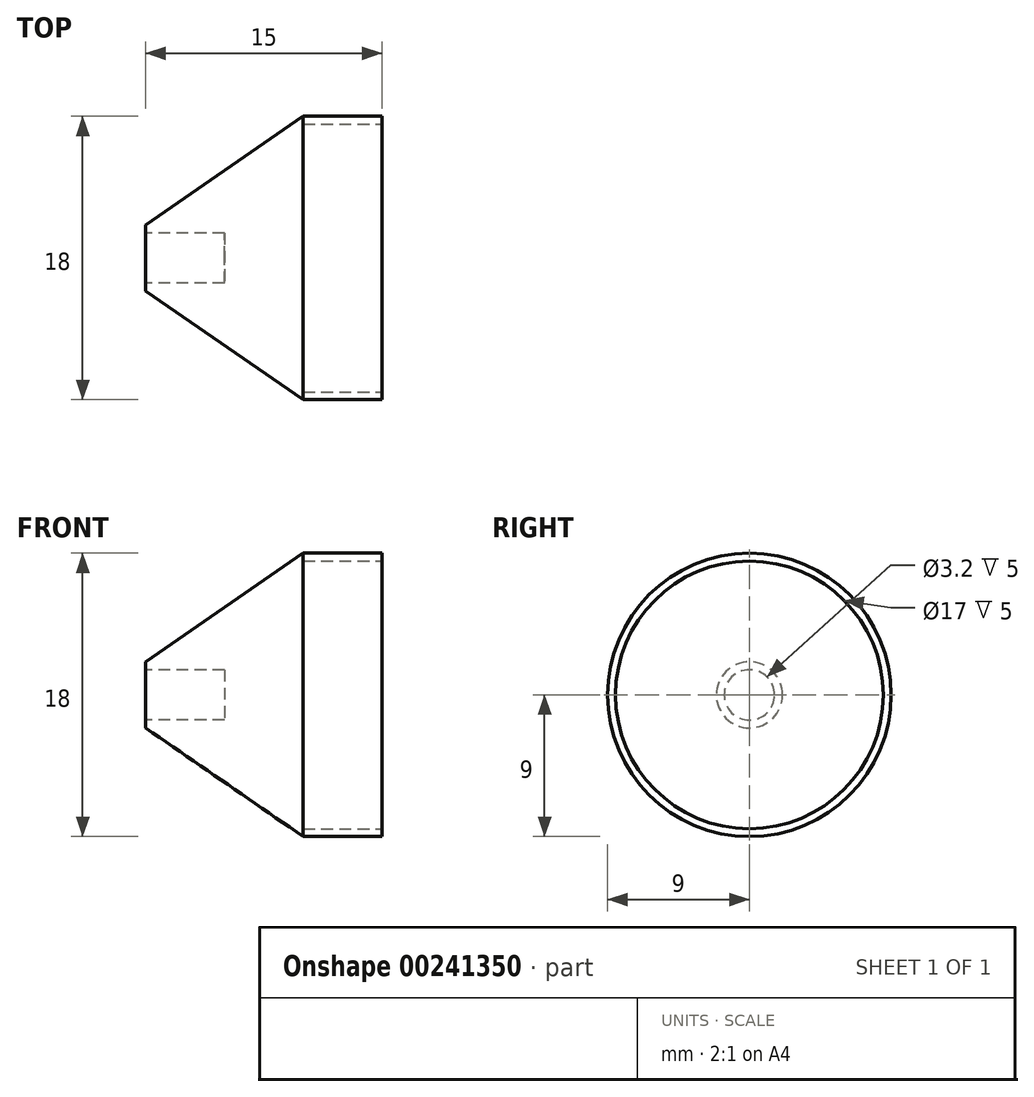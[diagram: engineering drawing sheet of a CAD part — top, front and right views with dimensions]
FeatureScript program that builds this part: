
annotation { "Feature Type Name" : "Feature", "Feature Type Description" : "" }
export const myFeature = defineFeature(function(context is Context, id is Id, definition is map)
    precondition{}
    {
        {
            var Q0;
            Q0=qCreatedBy(makeId("Right.planeOp"),FACE);
            var sketch = newSketch(context, id + "F0", { "sketchPlane" : qUnion([Q0])});
            skCircle(sketch, "E0", {"center": v(0, 0) * mm, "radius": 2.1 * mm});
            skSolve(sketch);
        }
        {
            var Q0;
            Q0=qCreatedBy(makeId("Right.planeOp"),FACE);
            cPlane(context, id + "F1", {"entities" : qUnion([Q0]), "cplaneType" : CPlaneType.OFFSET, "offset" : 10 * mm, "width" : 150 * mm, "height" : 150 * mm});
        }
        {
            var Q0;
            Q0=qCreatedBy(id+"F1.planeOp",FACE);
            var sketch = newSketch(context, id + "F2", { "sketchPlane" : qUnion([Q0])});
            skCircle(sketch, "E1", {"center": v(0, 0) * mm, "radius": 9 * mm});
            skSolve(sketch);
        }
        {
            var Q0;
            Q0 = qSketchRegion(id + "F0", true);
            var Q1;
            Q1 = qSketchRegion(id + "F2", true);
            loft(context, id + "F3", {"sheetProfilesArray" : [{ "sheetProfileEntities" : qUnion([Q0]) }, { "sheetProfileEntities" : qUnion([Q1]) }]});
        }
        {
            var Q0;
            Q0=makeQuery(id+"F3.opLoft","CAP_FACE",FACE,{"disambiguationData":[OSD([makeQuery(id+"F0.imprint","IMPRINT",FACE,{"disambiguationData":[TD([[makeQuery(id+"F0.imprint","IMPRINT",EDGE,{"derivedFrom":sQuery(id+"F0.wireOp",EDGE,"E0")}),1.0]])]})])],"isStart":true});
            var sketch = newSketch(context, id + "F4", { "sketchPlane" : qUnion([Q0])});
            skCircle(sketch, "E2", {"center": v(0, 0) * mm, "radius": 1.6 * mm});
            skSolve(sketch);
        }
        {
            var Q0;
            Q0 = qSketchRegion(id + "F4", true);
            extrude(context, id + "F5", {"entities" : qUnion([Q0]), "operationType" : NewBodyOperationType.REMOVE, "oppositeDirection" : true, "depth" : 5 * mm});
        }
        {
            var Q0;
            Q0 = qSketchRegion(id + "F2", true);
            extrude(context, id + "F6", {"entities" : qUnion([Q0]), "operationType" : NewBodyOperationType.ADD, "depth" : 5 * mm});
        }
        {
            var Q0;
            Q0=makeQuery(id+"F6.opExtrude","CAP_FACE",FACE,{"disambiguationData":[OSD([sQuery(id+"F2.wireOp",EDGE,"E1")])],"isStart":false});
            var sketch = newSketch(context, id + "F7", { "sketchPlane" : qUnion([Q0])});
            skCircle(sketch, "E3", {"center": v(0, 0) * mm, "radius": 8.5 * mm});
            skSolve(sketch);
        }
        {
            var Q0;
            Q0 = qSketchRegion(id + "F7", true);
            extrude(context, id + "F8", {"entities" : qUnion([Q0]), "operationType" : NewBodyOperationType.REMOVE, "oppositeDirection" : true, "depth" : 5 * mm});
        }
    });
